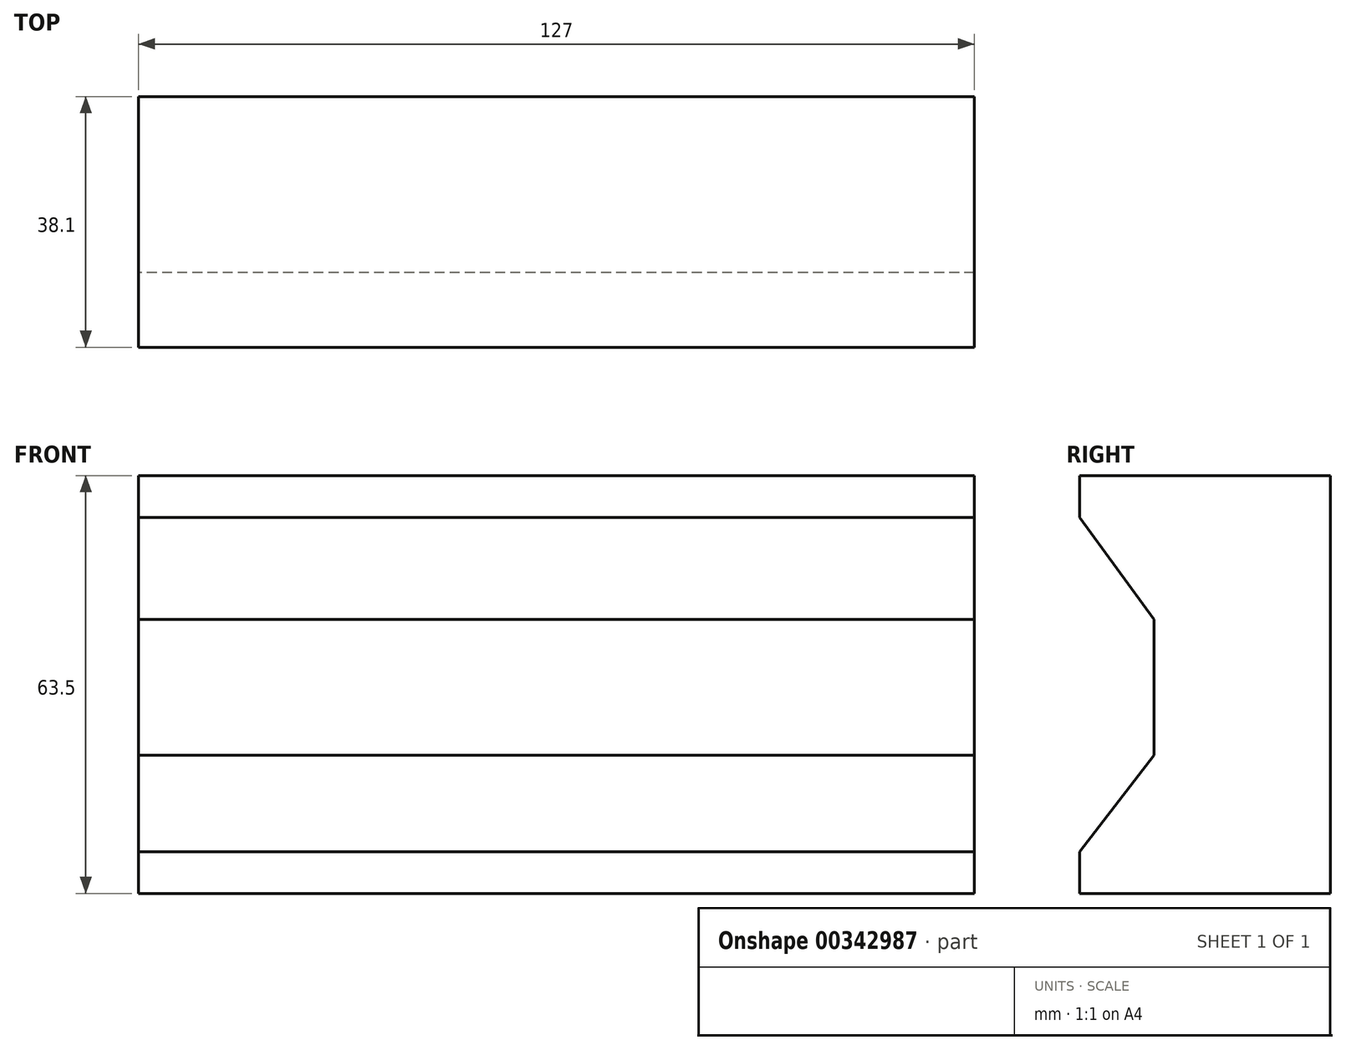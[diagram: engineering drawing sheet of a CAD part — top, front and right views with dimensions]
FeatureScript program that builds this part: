
annotation { "Feature Type Name" : "Feature", "Feature Type Description" : "" }
export const myFeature = defineFeature(function(context is Context, id is Id, definition is map)
    precondition{}
    {
        {
            var Q0;
            Q0=qCreatedBy(makeId("Right.planeOp"),FACE);
            var sketch = newSketch(context, id + "F0", { "sketchPlane" : qUnion([Q0])});
            skLineSegment(sketch, "E0", {"start": v(51.17, 6.35) * mm, "end": v(51.17, -57.15) * mm});
            skLineSegment(sketch, "E1", {"start": v(51.17, 6.35) * mm, "end": v(13.07, 6.35) * mm});
            skLineSegment(sketch, "E2", {"start": v(13.07, 6.35) * mm, "end": v(13.07, 0) * mm});
            skLineSegment(sketch, "E3", {"start": v(13.07, 0) * mm, "end": v(24.4, -15.53) * mm});
            skLineSegment(sketch, "E4", {"start": v(51.17, -57.15) * mm, "end": v(13.07, -57.15) * mm});
            skLineSegment(sketch, "E5", {"start": v(13.07, -57.15) * mm, "end": v(13.07, -50.8) * mm});
            skLineSegment(sketch, "E6", {"start": v(24.4, -15.53) * mm, "end": v(24.4, -36.15) * mm});
            skLineSegment(sketch, "E7", {"start": v(24.4, -36.15) * mm, "end": v(13.07, -50.8) * mm});
            skSolve(sketch);
        }
        {
            var Q0;
            Q0=makeQuery(id+"F0.imprint","IMPRINT",FACE,{"disambiguationData":[TD([[makeQuery(id+"F0.imprint","IMPRINT",EDGE,{"derivedFrom":sQuery(id+"F0.wireOp",EDGE,"E0")}),-1.0]])]});
            extrude(context, id + "F1", {"entities" : qUnion([Q0]), "depth" : 127 * mm});
        }
    });
